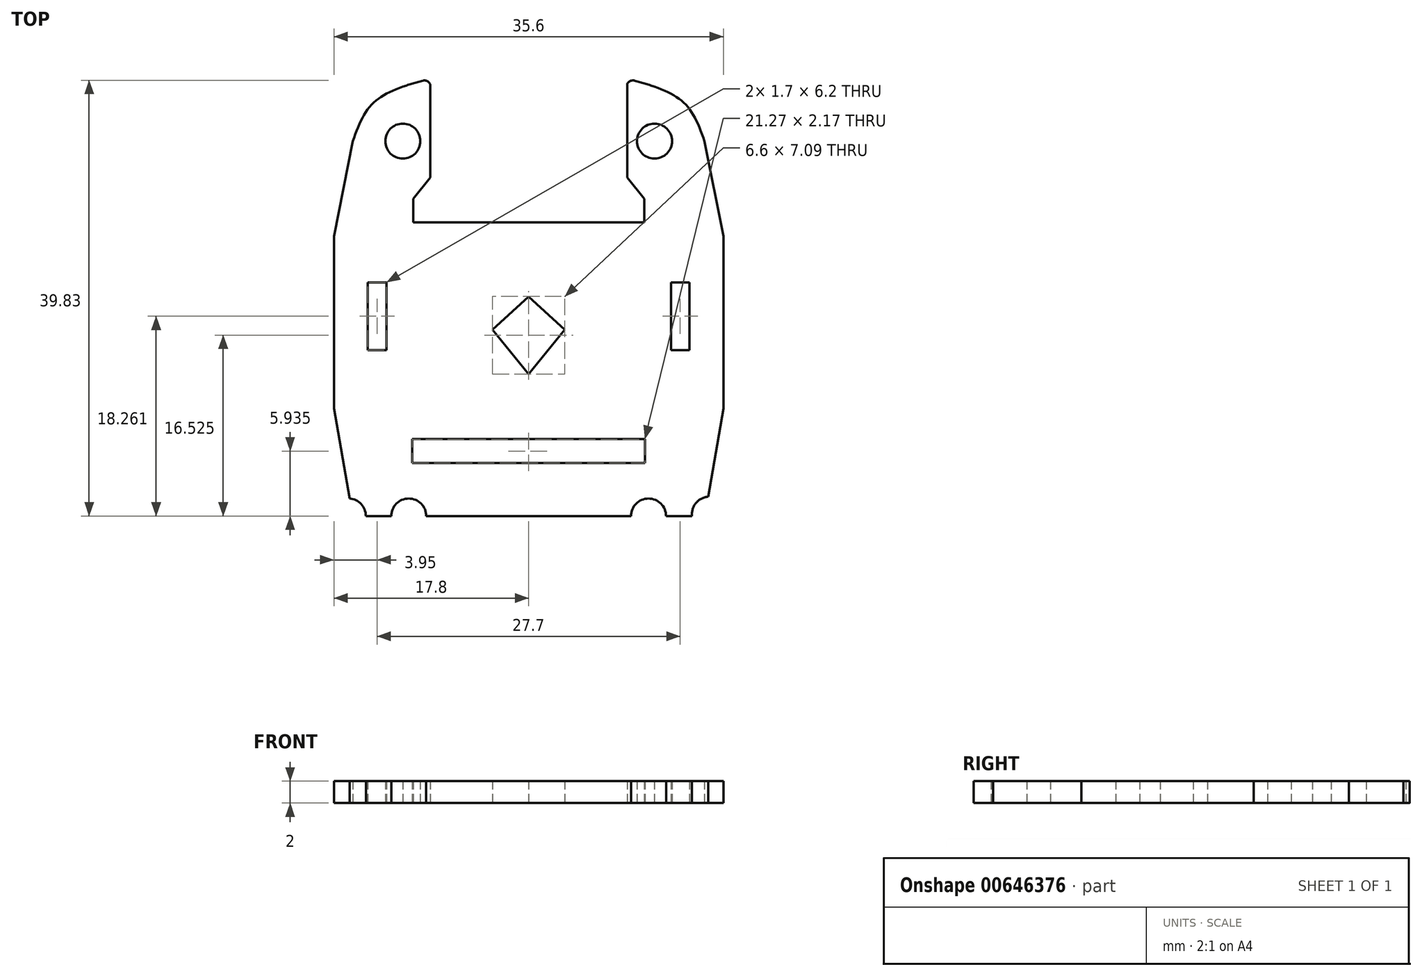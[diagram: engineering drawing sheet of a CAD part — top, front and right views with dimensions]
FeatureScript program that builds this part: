
annotation { "Feature Type Name" : "Feature", "Feature Type Description" : "" }
export const myFeature = defineFeature(function(context is Context, id is Id, definition is map)
    precondition{}
    {
        {
            var Q0;
            Q0=qCreatedBy(makeId("Top.planeOp"),FACE);
            var sketch = newSketch(context, id + "F0", { "sketchPlane" : qUnion([Q0])});
            skPoint(sketch, "E0", {"position": v(10.53, 34.52) * mm});
            skPoint(sketch, "E1", {"position": v(21.97, 0) * mm});
            skPoint(sketch, "E2", {"position": v(22.03, 34.57) * mm});
            skCircle(sketch, "E3", {"center": v(10.53, 34.52) * mm, "radius": 1.6 * mm});
            skPoint(sketch, "E4.endSnap0", {"position": v(0, 17.29) * mm});
            skCircle(sketch, "E5.MirrorC", {"center": v(11.07, 0.24) * mm, "radius": 1.6 * mm});
            skPoint(sketch, "E6", {"position": v(22.03, 17.29) * mm});
            skLineSegment(sketch, "E7", {"start": v(22.03, 13.22) * mm, "end": v(22.03, 7.19) * mm});
            skArc(sketch, "E8.0", {"start": v(5.97, 0) * mm, "mid": v(7.47, -3.6) * mm, "end": v(11.07, -5.1) * mm});
            skPoint(sketch, "E9", {"position": v(10.53, 39.5) * mm});
            skPoint(sketch, "E10", {"position": v(5.96, 34.52) * mm});
            skPoint(sketch, "E11", {"position": v(5.97, 0) * mm});
            skPoint(sketch, "E12.MirrorP", {"position": v(33.53, 34.52) * mm});
            skCircle(sketch, "E13.MirrorC", {"center": v(33.53, 34.52) * mm, "radius": 1.6 * mm});
            skArc(sketch, "E14.MirrorC", {"start": v(38.09, 0) * mm, "mid": v(36.6, -3.6) * mm, "end": v(32.99, -5.1) * mm});
            skCircle(sketch, "E15.MirrorC", {"center": v(32.99, 0.23) * mm, "radius": 1.6 * mm});
            skPoint(sketch, "E16.MirrorP", {"position": v(33.53, 39.5) * mm});
            skPoint(sketch, "E17.MirrorP", {"position": v(38.09, 0) * mm});
            skArc(sketch, "E18", {"start": v(33.53, 39.5) * mm, "mid": v(32.62, 39.78) * mm, "end": v(31.7, 40.05) * mm});
            skFitSpline(sketch, "E19", {"points": [v(5.96, 34.52) * mm, v(7.62, 37.8) * mm, v(10.53, 39.5) * mm], "startDerivative": vector(2.52, 7.3) * mm, "endDerivative": vector(7.64, 2.94) * mm});
            skArc(sketch, "E20.trimOffspring", {"start": v(12.36, 40.05) * mm, "mid": v(11.44, 39.78) * mm, "end": v(10.53, 39.5) * mm});
            skPoint(sketch, "E21.orphan", {"position": v(14.8, 40.62) * mm});
            skArc(sketch, "E22.MirrorCS", {"start": v(31.7, 40.05) * mm, "mid": v(32.62, 39.78) * mm, "end": v(33.53, 39.5) * mm});
            skPoint(sketch, "E23.MirrorP", {"position": v(29.26, 40.62) * mm});
            skPoint(sketch, "E24", {"position": v(22.03, 28.18) * mm});
            skLineSegment(sketch, "E25.bottom", {"start": v(32.6, 27.1) * mm, "end": v(11.47, 27.1) * mm});
            skLineSegment(sketch, "E25.left", {"start": v(32.6, 27.1) * mm, "end": v(32.6, 29.26) * mm});
            skLineSegment(sketch, "E25.right", {"start": v(11.47, 27.1) * mm, "end": v(11.47, 29.26) * mm});
            skLineSegment(sketch, "E26", {"start": v(22.03, 28.18) * mm, "end": v(22.03, 20.3) * mm});
            skPoint(sketch, "E27", {"position": v(21.96, 6.17) * mm});
            skLineSegment(sketch, "E28.bottom", {"start": v(32.52, 5.09) * mm, "end": v(11.4, 5.09) * mm});
            skLineSegment(sketch, "E28.top", {"start": v(32.52, 7.26) * mm, "end": v(11.4, 7.26) * mm});
            skLineSegment(sketch, "E28.right", {"start": v(11.4, 5.09) * mm, "end": v(11.4, 7.26) * mm});
            skPoint(sketch, "E29.MirrorP", {"position": v(5.97, 17.29) * mm});
            skPoint(sketch, "E30.orphan", {"position": v(4.88, 27.8) * mm});
            skPoint(sketch, "E31.orphan", {"position": v(4.88, 6.77) * mm});
            skPoint(sketch, "E32", {"position": v(11.07, -5.1) * mm});
            skLineSegment(sketch, "E33", {"start": v(11.07, -5.1) * mm, "end": v(23.21, -5.1) * mm});
            skCircle(sketch, "E34.MirrorC", {"center": v(32.99, 0.24) * mm, "radius": 1.6 * mm});
            skPoint(sketch, "E35.MirrorP", {"position": v(22.09, 0) * mm});
            skPoint(sketch, "E36.MirrorP", {"position": v(32.99, -5.1) * mm});
            skLineSegment(sketch, "E37.MirrorCS", {"start": v(32.99, -5.1) * mm, "end": v(20.85, -5.1) * mm});
            skPoint(sketch, "E38.orphan", {"position": v(2.03, -5.1) * mm});
            skPoint(sketch, "E39.MirrorCS.end.orphan", {"position": v(42.03, -5.1) * mm});
            skPoint(sketch, "E40", {"position": v(7.78, 18.5) * mm});
            skLineSegment(sketch, "E41", {"start": v(5.96, 34.52) * mm, "end": v(4.23, 25.82) * mm});
            skPoint(sketch, "E41.endSnap0", {"position": v(5.23, 18.5) * mm});
            skLineSegment(sketch, "E42", {"start": v(4.23, 10.08) * mm, "end": v(5.97, 0) * mm});
            skLineSegment(sketch, "E43.MirrorCS", {"start": v(32.66, 5.09) * mm, "end": v(32.66, 7.26) * mm});
            skFitSpline(sketch, "E44.MirrorCS", {"points": [v(38.1, 34.52) * mm, v(36.44, 37.8) * mm, v(33.53, 39.5) * mm], "startDerivative": vector(-2.52, 7.3) * mm, "endDerivative": vector(-7.64, 2.94) * mm});
            skLineSegment(sketch, "E45.MirrorCS", {"start": v(38.1, 34.52) * mm, "end": v(39.83, 25.82) * mm});
            skPoint(sketch, "E46.MirrorP", {"position": v(39.18, 6.77) * mm});
            skLineSegment(sketch, "E47.MirrorCS", {"start": v(11.47, 27.1) * mm, "end": v(32.6, 27.1) * mm});
            skPoint(sketch, "E48.MirrorP", {"position": v(39.18, 27.8) * mm});
            skPoint(sketch, "E49.MirrorP", {"position": v(44.06, 17.29) * mm});
            skLineSegment(sketch, "E50.MirrorCS", {"start": v(39.83, 10.08) * mm, "end": v(38.09, 0) * mm});
            skLineSegment(sketch, "E51.MirrorCS", {"start": v(11.54, 5.09) * mm, "end": v(32.66, 5.09) * mm});
            skLineSegment(sketch, "E52.MirrorCS", {"start": v(11.54, 7.26) * mm, "end": v(32.66, 7.26) * mm});
            skLineSegment(sketch, "E53", {"start": v(39.83, 25.82) * mm, "end": v(39.83, 10.08) * mm});
            skPoint(sketch, "E54.orphan", {"position": v(41.29, 18.5) * mm});
            skLineSegment(sketch, "E55.MirrorCS", {"start": v(7.33, 15.4) * mm, "end": v(8.18, 15.4) * mm});
            skLineSegment(sketch, "E56.MirrorCS", {"start": v(7.33, 21.6) * mm, "end": v(8.18, 21.6) * mm});
            skLineSegment(sketch, "E57.MirrorCS", {"start": v(4.23, 25.82) * mm, "end": v(4.23, 10.08) * mm});
            skPoint(sketch, "E58.MirrorP", {"position": v(2.77, 18.5) * mm});
            skPoint(sketch, "E59.endSnap0", {"position": v(22.03, 35.8) * mm});
            skPoint(sketch, "E60.orphan", {"position": v(22.03, 37.04) * mm});
            skPoint(sketch, "E61.MirrorCS.end.orphan", {"position": v(28.37, 40.18) * mm});
            skPoint(sketch, "E61.MirrorCS.start.orphan", {"position": v(30.4, 40.37) * mm});
            skPoint(sketch, "E62.end.orphan", {"position": v(15.69, 40.18) * mm});
            skPoint(sketch, "E63.orphan", {"position": v(13.67, 40.37) * mm});
            skLineSegment(sketch, "E64", {"start": v(22.03, 20.3) * mm, "end": v(25.33, 17.29) * mm});
            skLineSegment(sketch, "E65", {"start": v(25.33, 17.29) * mm, "end": v(22.03, 13.22) * mm});
            skLineSegment(sketch, "E66.MirrorCS", {"start": v(18.73, 17.29) * mm, "end": v(22.03, 13.22) * mm});
            skLineSegment(sketch, "E67.MirrorCS", {"start": v(22.03, 20.3) * mm, "end": v(18.73, 17.29) * mm});
            skPoint(sketch, "E68.MirrorP", {"position": v(38.83, 18.5) * mm});
            skLineSegment(sketch, "E69", {"start": v(7.33, 21.6) * mm, "end": v(7.33, 15.4) * mm});
            skLineSegment(sketch, "E70.MirrorCS", {"start": v(9.03, 15.4) * mm, "end": v(8.18, 15.4) * mm});
            skLineSegment(sketch, "E71.MirrorCS", {"start": v(9.03, 21.6) * mm, "end": v(8.18, 21.6) * mm});
            skLineSegment(sketch, "E72.MirrorCS", {"start": v(9.03, 21.6) * mm, "end": v(9.03, 15.4) * mm});
            skPoint(sketch, "E73.orphan", {"position": v(9.88, 15.4) * mm});
            skPoint(sketch, "E74.orphan", {"position": v(9.88, 21.6) * mm});
            skPoint(sketch, "E75.orphan", {"position": v(6.48, 21.6) * mm});
            skPoint(sketch, "E76.orphan", {"position": v(6.48, 15.4) * mm});
            skPoint(sketch, "E77.MirrorP", {"position": v(36.28, 18.5) * mm});
            skLineSegment(sketch, "E78.MirrorCS", {"start": v(35.03, 21.6) * mm, "end": v(35.88, 21.6) * mm});
            skLineSegment(sketch, "E79.MirrorCS", {"start": v(35.03, 15.4) * mm, "end": v(35.88, 15.4) * mm});
            skLineSegment(sketch, "E80.MirrorCS", {"start": v(36.73, 21.6) * mm, "end": v(35.88, 21.6) * mm});
            skLineSegment(sketch, "E81.MirrorCS", {"start": v(36.73, 15.4) * mm, "end": v(35.88, 15.4) * mm});
            skPoint(sketch, "E82.MirrorP", {"position": v(38.09, 17.29) * mm});
            skLineSegment(sketch, "E83.MirrorCS", {"start": v(35.03, 21.6) * mm, "end": v(35.03, 15.4) * mm});
            skPoint(sketch, "E84.MirrorP", {"position": v(34.18, 21.6) * mm});
            skPoint(sketch, "E85.MirrorP", {"position": v(34.18, 15.4) * mm});
            skLineSegment(sketch, "E86.MirrorCS", {"start": v(36.73, 21.6) * mm, "end": v(36.73, 15.4) * mm});
            skPoint(sketch, "E87.MirrorP", {"position": v(37.58, 21.6) * mm});
            skPoint(sketch, "E88.MirrorP", {"position": v(37.58, 15.4) * mm});
            skLineSegment(sketch, "E89", {"start": v(13.03, 34.52) * mm, "end": v(13.03, 39.72) * mm});
            skLineSegment(sketch, "E90", {"start": v(13.03, 39.72) * mm, "end": v(13.03, 31.19) * mm});
            skLineSegment(sketch, "E91", {"start": v(11.47, 29.26) * mm, "end": v(13.03, 31.19) * mm});
            skPoint(sketch, "E92.orphan", {"position": v(22.03, 35.26) * mm});
            skArc(sketch, "E93", {"start": v(12.36, 40.05) * mm, "mid": v(12.76, 40) * mm, "end": v(13.03, 39.72) * mm});
            skArc(sketch, "E94.MirrorCS", {"start": v(31.7, 40.05) * mm, "mid": v(31.3, 40) * mm, "end": v(31.03, 39.72) * mm});
            skLineSegment(sketch, "E95.MirrorCS", {"start": v(31.03, 34.52) * mm, "end": v(31.03, 39.72) * mm});
            skLineSegment(sketch, "E96.MirrorCS", {"start": v(32.6, 29.26) * mm, "end": v(31.03, 31.19) * mm});
            skLineSegment(sketch, "E97.MirrorCS", {"start": v(31.03, 39.72) * mm, "end": v(31.03, 31.19) * mm});
            skLineSegment(sketch, "E98", {"start": v(22.03, 4.33) * mm, "end": v(22.09, -6.8) * mm});
            skLineSegment(sketch, "E99", {"start": v(2.92, 0.24) * mm, "end": v(56.93, 0.24) * mm});
            skPoint(sketch, "E100", {"position": v(5.55, 0.24) * mm});
            skPoint(sketch, "E101.MirrorP", {"position": v(38.55, 0.4) * mm});
            skCircle(sketch, "E102", {"center": v(5.55, 0.24) * mm, "radius": 1.6 * mm});
            skCircle(sketch, "E103", {"center": v(38.55, 0.4) * mm, "radius": 1.6 * mm});
            skLineSegment(sketch, "E104", {"start": v(39.83, 10.08) * mm, "end": v(42.03, -5.1) * mm});
            skSolve(sketch);
        }
        {
            var Q0;
            Q0=makeQuery(id+"F0.imprint","IMPRINT",FACE,{"disambiguationData":[TD([[makeQuery(id+"F0.imprint","IMPRINT",EDGE,{"derivedFrom":sQuery(id+"F0.wireOp",EDGE,"E3")}),-1.0]])]});
            extrude(context, id + "F1", {"entities" : qUnion([Q0]), "depth" : 2 * mm, "offsetDistance" : 25 * mm});
        }
    });
